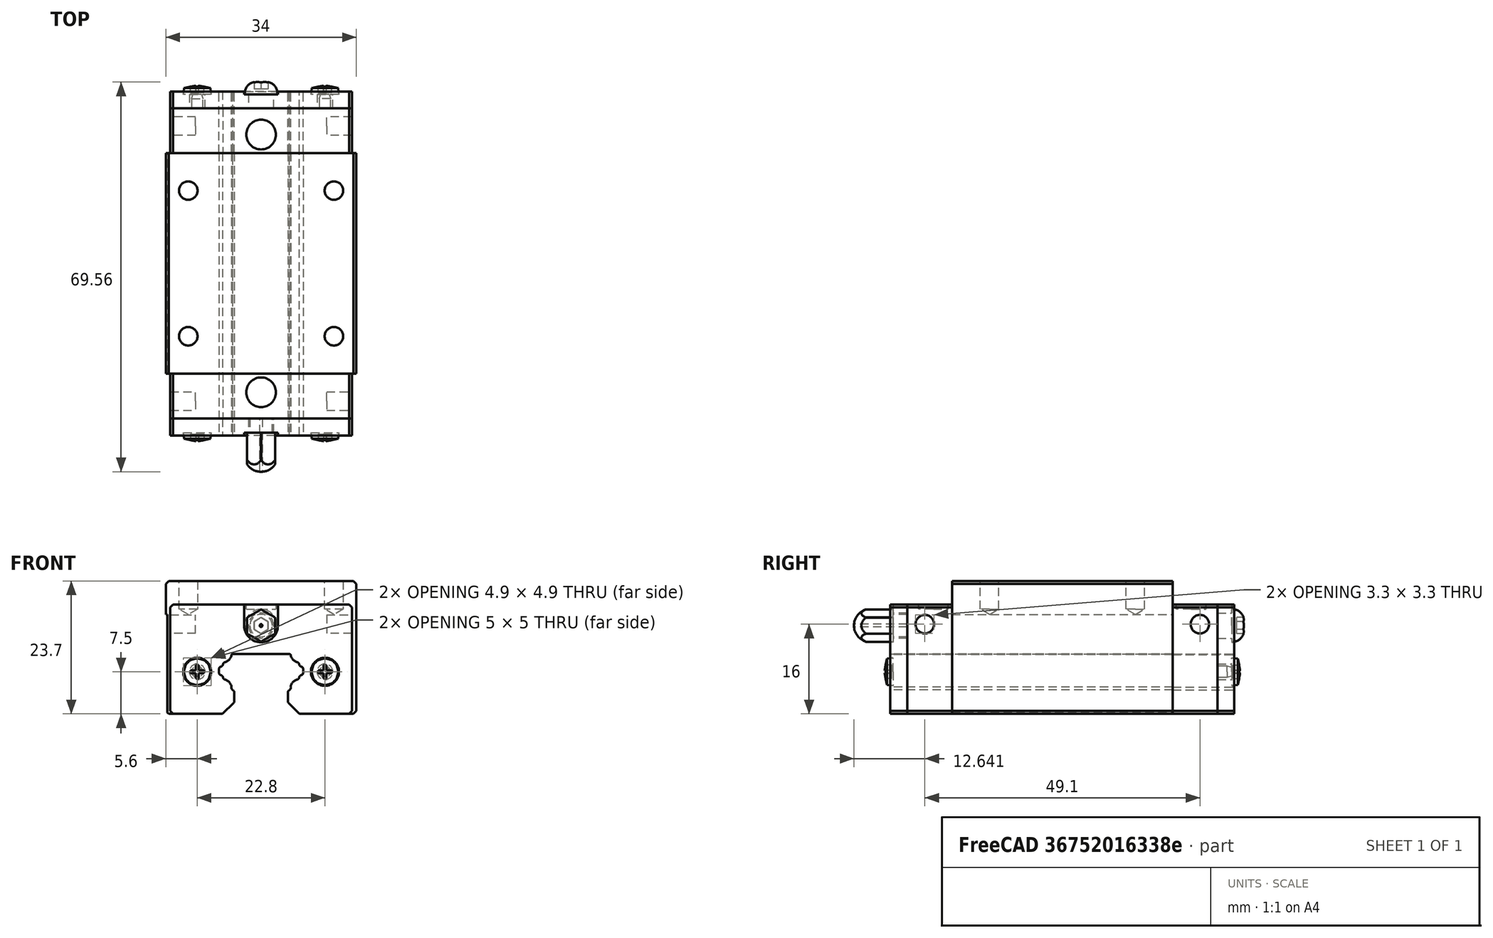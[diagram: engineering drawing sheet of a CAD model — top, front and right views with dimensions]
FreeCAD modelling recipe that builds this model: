
FCSTD DOCUMENT  (FreeCAD 0.21R38887 (Git))
Label: HGH15CA
License: All rights reserved
LicenseURL: http://en.wikipedia.org/wiki/All_rights_reserved
objects: Part::FeaturePython×8, App::FeaturePython×2, Part::Feature×1
note: 8 computed .brp shape members not serialized (recipe doc carries the construction recipe); baked Part::Feature solids carry a one-line shape summary decoded from their .brp

FEATURE [App::FeaturePython] Constraints  # WARN: FeaturePython — macro-defined, semantics opaque (R4)
  TreeRank = 3
  _LinkVersion = 1
  _Version = 1
FEATURE [Part::Feature] Solid  label="HGH15CAZ0H_FILE"
  InvalidShape = false
  TreeRank = 12
  ValidateShape = false
  shape: bbox 34 x 69.56 x 23.7 mm, 296 faces (baked)
FEATURE [Part::FeaturePython] Parts  label="HGH15CAZ0H"  # WARN: FeaturePython — macro-defined, semantics opaque (R4)
  Group = -> [Solid]
  GroupMode = 0
  InvalidShape = false
  TreeRank = 5
  ValidateShape = false
  _LinkVersion = 1
FEATURE [Part::FeaturePython] Assembly  label="HGH15CA"  # WARN: FeaturePython — macro-defined, semantics opaque (R4)
  AutoRelax = true
  BuildShape = 0
  Freeze = false
  Group = -> [Constraints,Elements,Parts]
  InvalidShape = false
  TreeRank = 2
  ValidateShape = false
  Verbose = false
  _LinkVersion = 1
  _SolverType = 1
  _Version = 1
FEATURE [App::FeaturePython] Elements  # WARN: FeaturePython — macro-defined, semantics opaque (R4)
  Group = -> [Element,Element001,Element002,Element003,Element004,Element005]
  TreeRank = 4
  _LinkVersion = 1
FEATURE [Part::FeaturePython] Element  label="ПлоскостьПрилегания"  # link proxy (typed FeaturePython)
  Detach = false
  InvalidShape = false
  LinkTransform = true
  LinkedObject = -> Solid [Face265]
  TreeRank = 6
  ValidateShape = false
  _LinkVersion = 1
  _Parent = -> Elements
FEATURE [Part::FeaturePython] Element001  label="БоковаяПласкостьПрилегания"  # link proxy (typed FeaturePython)
  Detach = false
  InvalidShape = false
  LinkTransform = true
  LinkedObject = -> Solid [Face253]
  TreeRank = 7
  ValidateShape = false
  _LinkVersion = 1
  _Parent = -> Elements
FEATURE [Part::FeaturePython] Element002  label="Отв1"  # link proxy (typed FeaturePython)
  Detach = false
  InvalidShape = false
  LinkTransform = true
  LinkedObject = -> Solid [Face261]
  TreeRank = 8
  ValidateShape = false
  _LinkVersion = 1
  _Parent = -> Elements
FEATURE [Part::FeaturePython] Element003  label="Отв2"  # link proxy (typed FeaturePython)
  Detach = false
  InvalidShape = false
  LinkTransform = true
  LinkedObject = -> Solid [Face257]
  TreeRank = 9
  ValidateShape = false
  _LinkVersion = 1
  _Parent = -> Elements
FEATURE [Part::FeaturePython] Element004  label="Отв3"  # link proxy (typed FeaturePython)
  Detach = false
  InvalidShape = false
  LinkTransform = true
  LinkedObject = -> Solid [Face263]
  TreeRank = 10
  ValidateShape = false
  _LinkVersion = 1
  _Parent = -> Elements
FEATURE [Part::FeaturePython] Element005  label="Отв4"  # link proxy (typed FeaturePython)
  Detach = false
  InvalidShape = false
  LinkTransform = true
  LinkedObject = -> Solid [Face259]
  TreeRank = 11
  ValidateShape = false
  _LinkVersion = 1
  _Parent = -> Elements
